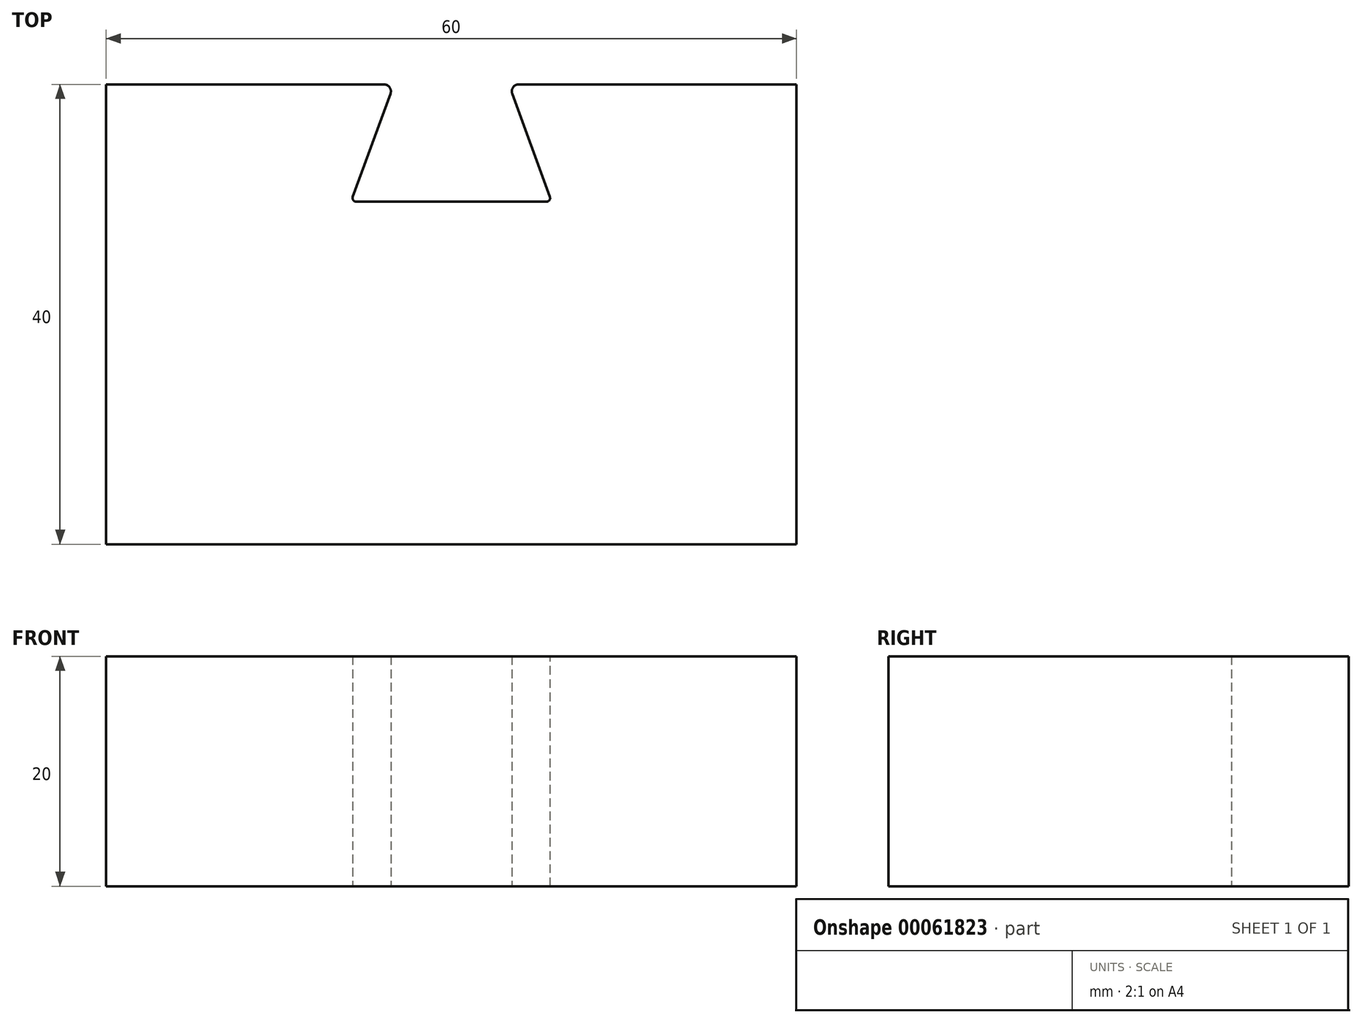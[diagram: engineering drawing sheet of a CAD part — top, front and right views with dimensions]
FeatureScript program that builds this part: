
annotation { "Feature Type Name" : "Feature", "Feature Type Description" : "" }
export const myFeature = defineFeature(function(context is Context, id is Id, definition is map)
    precondition{}
    {
        {
            var Q0;
            Q0=qCreatedBy(makeId("Top.planeOp"),FACE);
            var sketch = newSketch(context, id + "F0", { "sketchPlane" : qUnion([Q0])});
            skLineSegment(sketch, "E0", {"start": v(0, 0) * mm, "end": v(-30, 0) * mm});
            skLineSegment(sketch, "E1", {"start": v(-30, 0) * mm, "end": v(-30, 40) * mm});
            skLineSegment(sketch, "E2", {"start": v(-30, 40) * mm, "end": v(-5, 40) * mm});
            skLineSegment(sketch, "E3", {"start": v(-5, 40) * mm, "end": v(-8.71, 29.8) * mm});
            skLineSegment(sketch, "E4", {"start": v(-8.71, 29.8) * mm, "end": v(0, 29.8) * mm});
            skLineSegment(sketch, "E5", {"start": v(0, 29.8) * mm, "end": v(0, 0) * mm, "construction": true});
            skLineSegment(sketch, "E6.MirrorCS", {"start": v(8.71, 29.8) * mm, "end": v(0, 29.8) * mm});
            skLineSegment(sketch, "E7.MirrorCS", {"start": v(5, 40) * mm, "end": v(8.71, 29.8) * mm});
            skLineSegment(sketch, "E8.MirrorCS", {"start": v(30, 40) * mm, "end": v(5, 40) * mm});
            skLineSegment(sketch, "E9.MirrorCS", {"start": v(0, 0) * mm, "end": v(30, 0) * mm});
            skLineSegment(sketch, "E10.MirrorCS", {"start": v(30, 0) * mm, "end": v(30, 40) * mm});
            skSolve(sketch);
        }
        {
            var Q0;
            Q0 = qSketchRegion(id + "F0", true);
            extrude(context, id + "F1", {"entities" : qUnion([Q0]), "endBound" : BoundingType.SYMMETRIC, "depth" : 20 * mm});
        }
        {
            var Q0;
            Q0=makeQuery(id+"F1.opExtrude","SWEPT_EDGE",EDGE,{"disambiguationData":[OSD([sQuery(id+"F0.wireOp",EDGE,"E2"),sQuery(id+"F0.wireOp",EDGE,"E3")])]});
            var Q1;
            Q1=makeQuery(id+"F1.opExtrude","SWEPT_EDGE",EDGE,{"disambiguationData":[OSD([sQuery(id+"F0.wireOp",EDGE,"E7.MirrorCS"),sQuery(id+"F0.wireOp",EDGE,"E8.MirrorCS")])]});
            fillet(context, id + "F2", {"entities" : qUnion([Q0, Q1]), "radius" : 0.6 * mm, "tangentPropagation" : true, "allowEdgeOverflow" : false});
        }
        {
            var Q0;
            Q0=makeQuery(id+"F1.opExtrude","SWEPT_EDGE",EDGE,{"disambiguationData":[OSD([sQuery(id+"F0.wireOp",EDGE,"E3"),sQuery(id+"F0.wireOp",EDGE,"E4")])]});
            var Q1;
            Q1=makeQuery(id+"F1.opExtrude","SWEPT_EDGE",EDGE,{"disambiguationData":[OSD([sQuery(id+"F0.wireOp",EDGE,"E6.MirrorCS"),sQuery(id+"F0.wireOp",EDGE,"E7.MirrorCS")])]});
            fillet(context, id + "F3", {"entities" : qUnion([Q0, Q1]), "radius" : 0.3 * mm, "tangentPropagation" : true, "allowEdgeOverflow" : false});
        }
    });
